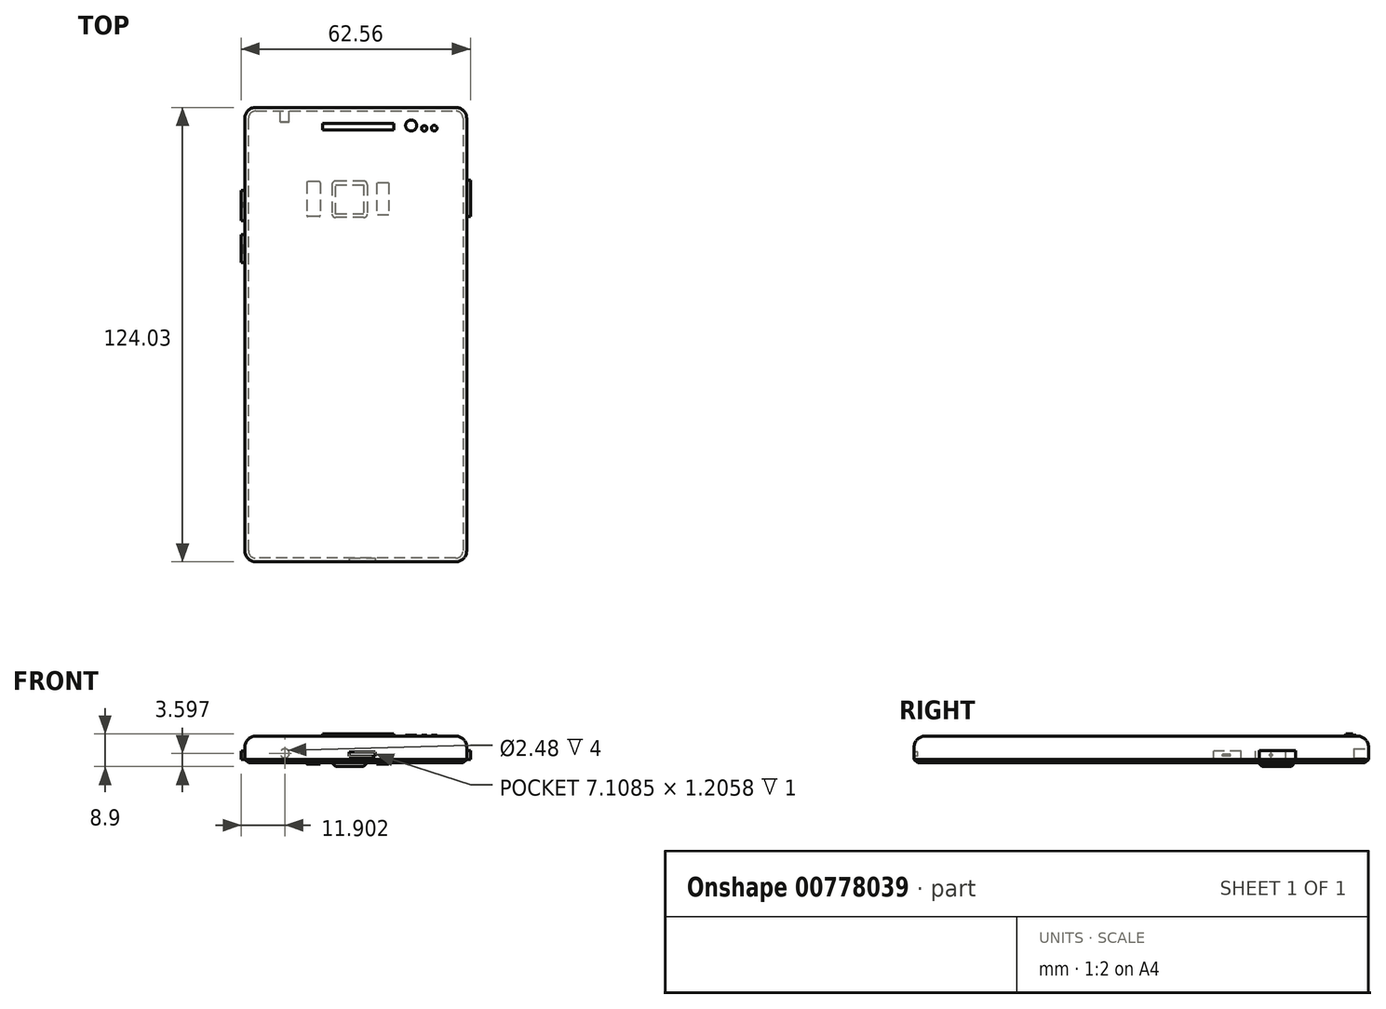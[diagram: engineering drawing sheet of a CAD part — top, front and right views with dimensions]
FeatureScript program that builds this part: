
annotation { "Feature Type Name" : "Feature", "Feature Type Description" : "" }
export const myFeature = defineFeature(function(context is Context, id is Id, definition is map)
    precondition{}
    {
        {
            var Q0;
            Q0=qCreatedBy(makeId("Top.planeOp"),FACE);
            var sketch = newSketch(context, id + "F0", { "sketchPlane" : qUnion([Q0])});
            skLineSegment(sketch, "E0.bottom", {"start": v(-27.17, 60.84) * mm, "end": v(33.39, 60.84) * mm});
            skLineSegment(sketch, "E0.top", {"start": v(-27.17, -63.19) * mm, "end": v(33.39, -63.19) * mm});
            skLineSegment(sketch, "E0.left", {"start": v(-27.17, 60.84) * mm, "end": v(-27.17, -63.19) * mm});
            skLineSegment(sketch, "E0.right", {"start": v(33.39, 60.84) * mm, "end": v(33.39, -63.19) * mm});
            skSolve(sketch);
        }
        {
            var Q0;
            Q0 = qSketchRegion(id + "F0", true);
            extrude(context, id + "F1", {"entities" : qUnion([Q0]), "depth" : 7.3 * mm, "offsetDistance" : 25 * mm});
        }
        {
            var Q0;
            Q0=makeQuery(id+"F1.opExtrude","CAP_EDGE",EDGE,{"disambiguationData":[OSD([sQuery(id+"F0.wireOp",EDGE,"E0.left")])],"isStart":false});
            var Q1;
            Q1=makeQuery(id+"F1.opExtrude","CAP_EDGE",EDGE,{"disambiguationData":[OSD([sQuery(id+"F0.wireOp",EDGE,"E0.right")])],"isStart":false});
            fillet(context, id + "F2", {"entities" : qUnion([Q0, Q1]), "radius" : 3 * mm, "tangentPropagation" : true, "allowEdgeOverflow" : false});
        }
        {
            var Q0;
            Q0=makeQuery(id+"F1.opExtrude","CAP_EDGE",EDGE,{"disambiguationData":[OSD([sQuery(id+"F0.wireOp",EDGE,"E0.bottom")])],"isStart":false});
            fillet(context, id + "F3", {"entities" : qUnion([Q0]), "radius" : 3 * mm, "tangentPropagation" : true, "allowEdgeOverflow" : false});
        }
        {
            var Q0;
            Q0=makeQuery(id+"F1.opExtrude","CAP_EDGE",EDGE,{"disambiguationData":[OSD([sQuery(id+"F0.wireOp",EDGE,"E0.top")])],"isStart":false});
            fillet(context, id + "F4", {"entities" : qUnion([Q0]), "radius" : 3 * mm, "tangentPropagation" : true, "allowEdgeOverflow" : false});
        }
        {
            var Q0;
            Q0=makeQuery(id+"F1.opExtrude","CAP_FACE",FACE,{"disambiguationData":[OSD([sQuery(id+"F0.wireOp",EDGE,"E0.bottom"),sQuery(id+"F0.wireOp",EDGE,"E0.top"),sQuery(id+"F0.wireOp",EDGE,"E0.left"),sQuery(id+"F0.wireOp",EDGE,"E0.right")])],"isStart":false});
            var sketch = newSketch(context, id + "F5", { "sketchPlane" : qUnion([Q0])});
            skLineSegment(sketch, "E1.bottom", {"start": v(-24.17, 57.84) * mm, "end": v(30.39, 57.84) * mm});
            skLineSegment(sketch, "E1.top", {"start": v(-24.17, 53.8) * mm, "end": v(30.39, 53.8) * mm});
            skLineSegment(sketch, "E1.left", {"start": v(-24.17, 57.84) * mm, "end": v(-24.17, 53.8) * mm});
            skLineSegment(sketch, "E1.right", {"start": v(30.39, 57.84) * mm, "end": v(30.39, 53.8) * mm});
            skSolve(sketch);
        }
        {
            var Q0;
            Q0=makeQuery(id+"F5.imprint","IMPRINT",FACE,{"disambiguationData":[TD([[makeQuery(id+"F5.imprint","IMPRINT",EDGE,{"derivedFrom":sQuery(id+"F5.wireOp",EDGE,"E1.bottom")}),1.0]])]});
            var sketch = newSketch(context, id + "F6", { "sketchPlane" : qUnion([Q0])});
            skLineSegment(sketch, "E2.bottom", {"start": v(-5.95, 56.51) * mm, "end": v(13.55, 56.51) * mm});
            skLineSegment(sketch, "E2.top", {"start": v(-5.95, 54.7) * mm, "end": v(13.55, 54.7) * mm});
            skLineSegment(sketch, "E2.left", {"start": v(-5.95, 56.51) * mm, "end": v(-5.95, 54.7) * mm});
            skLineSegment(sketch, "E2.right", {"start": v(13.55, 56.51) * mm, "end": v(13.55, 54.7) * mm});
            skSolve(sketch);
        }
        {
            var Q0;
            Q0=makeQuery(id+"F6.imprint","IMPRINT",FACE,{"disambiguationData":[TD([[makeQuery(id+"F6.imprint","IMPRINT",EDGE,{"derivedFrom":sQuery(id+"F6.wireOp",EDGE,"E2.bottom")}),-1.0]])]});
            extrude(context, id + "F7", {"entities" : qUnion([Q0]), "operationType" : NewBodyOperationType.ADD, "depth" : 0.3 * mm, "offsetDistance" : 25 * mm});
        }
        {
            var Q0;
            Q0=makeQuery(id+"F5.imprint","IMPRINT",FACE,{"disambiguationData":[TD([[makeQuery(id+"F5.imprint","IMPRINT",EDGE,{"derivedFrom":sQuery(id+"F5.wireOp",EDGE,"E1.bottom")}),1.0]])]});
            var sketch = newSketch(context, id + "F8", { "sketchPlane" : qUnion([Q0])});
            skCircle(sketch, "E3", {"center": v(18.23, 55.9) * mm, "radius": 1.51 * mm});
            skCircle(sketch, "E4", {"center": v(21.8, 55.1) * mm, "radius": 0.75 * mm});
            skCircle(sketch, "E5", {"center": v(24.52, 55.17) * mm, "radius": 0.77 * mm});
            skSolve(sketch);
        }
        {
            var Q0;
            Q0=makeQuery(id+"F8.imprint","IMPRINT",FACE,{"disambiguationData":[TD([[makeQuery(id+"F8.imprint","IMPRINT",EDGE,{"derivedFrom":sQuery(id+"F8.wireOp",EDGE,"E3")}),1.0]])]});
            var Q1;
            Q1=makeQuery(id+"F8.imprint","IMPRINT",FACE,{"disambiguationData":[TD([[makeQuery(id+"F8.imprint","IMPRINT",EDGE,{"derivedFrom":sQuery(id+"F8.wireOp",EDGE,"E4")}),1.0]])]});
            var Q2;
            Q2=makeQuery(id+"F8.imprint","IMPRINT",FACE,{"disambiguationData":[TD([[makeQuery(id+"F8.imprint","IMPRINT",EDGE,{"derivedFrom":sQuery(id+"F8.wireOp",EDGE,"E5")}),1.0]])]});
            var Q3;
            Q3=makeQuery(id+"F7.opExtrude","CAP_FACE",FACE,{"disambiguationData":[OSD([sQuery(id+"F6.wireOp",EDGE,"E2.bottom"),sQuery(id+"F6.wireOp",EDGE,"E2.top"),sQuery(id+"F6.wireOp",EDGE,"E2.left"),sQuery(id+"F6.wireOp",EDGE,"E2.right")])],"isStart":false});
            extrude(context, id + "F9", {"entities" : qUnion([Q0, Q1, Q2, Q3]), "operationType" : NewBodyOperationType.ADD, "depth" : 0.3 * mm, "offsetDistance" : 25 * mm});
        }
        {
            var Q0;
            Q0=makeQuery(id+"F1.opExtrude","CAP_EDGE",EDGE,{"disambiguationData":[OSD([sQuery(id+"F0.wireOp",EDGE,"E0.right")])],"isStart":true});
            var Q1;
            Q1=makeQuery(id+"F1.opExtrude","CAP_EDGE",EDGE,{"disambiguationData":[OSD([sQuery(id+"F0.wireOp",EDGE,"E0.bottom")])],"isStart":true});
            var Q2;
            Q2=makeQuery(id+"F1.opExtrude","CAP_EDGE",EDGE,{"disambiguationData":[OSD([sQuery(id+"F0.wireOp",EDGE,"E0.left")])],"isStart":true});
            var Q3;
            Q3=makeQuery(id+"F1.opExtrude","CAP_FACE",FACE,{"disambiguationData":[OSD([sQuery(id+"F0.wireOp",EDGE,"E0.bottom"),sQuery(id+"F0.wireOp",EDGE,"E0.top"),sQuery(id+"F0.wireOp",EDGE,"E0.left"),sQuery(id+"F0.wireOp",EDGE,"E0.right")])],"isStart":true});
            chamfer(context, id + "F10", {"entities" : qUnion([Q0, Q1, Q2, Q3]), "width" : 1 * mm, "tangentPropagation" : true});
        }
        {
            var Q0;
            Q0=makeQuery(id+"F1.opExtrude","CAP_FACE",FACE,{"disambiguationData":[OSD([sQuery(id+"F0.wireOp",EDGE,"E0.bottom"),sQuery(id+"F0.wireOp",EDGE,"E0.top"),sQuery(id+"F0.wireOp",EDGE,"E0.left"),sQuery(id+"F0.wireOp",EDGE,"E0.right")])],"isStart":true});
            var sketch = newSketch(context, id + "F11", { "sketchPlane" : qUnion([Q0])});
            skLineSegment(sketch, "E6.bottom", {"start": v(6.26, -40.74) * mm, "end": v(-3.36, -40.74) * mm});
            skLineSegment(sketch, "E6.top", {"start": v(6.26, -30.76) * mm, "end": v(-3.36, -30.76) * mm});
            skLineSegment(sketch, "E6.left", {"start": v(6.26, -40.74) * mm, "end": v(6.26, -30.76) * mm});
            skLineSegment(sketch, "E6.right", {"start": v(-3.36, -40.74) * mm, "end": v(-3.36, -30.76) * mm});
            skSolve(sketch);
        }
        {
            var Q0;
            Q0 = qSketchRegion(id + "F11", true);
            extrude(context, id + "F12", {"entities" : qUnion([Q0]), "operationType" : NewBodyOperationType.ADD, "depth" : 1 * mm, "offsetDistance" : 25 * mm});
        }
        {
            var Q0;
            Q0=makeQuery(id+"F12.opExtrude","SWEPT_EDGE",EDGE,{"disambiguationData":[OSD([sQuery(id+"F11.wireOp",EDGE,"E6.bottom"),sQuery(id+"F11.wireOp",EDGE,"E6.right")])]});
            var Q1;
            Q1=makeQuery(id+"F12.opExtrude","SWEPT_EDGE",EDGE,{"disambiguationData":[OSD([sQuery(id+"F11.wireOp",EDGE,"E6.top"),sQuery(id+"F11.wireOp",EDGE,"E6.right")])]});
            var Q2;
            Q2=makeQuery(id+"F12.opExtrude","SWEPT_EDGE",EDGE,{"disambiguationData":[OSD([sQuery(id+"F11.wireOp",EDGE,"E6.top"),sQuery(id+"F11.wireOp",EDGE,"E6.left")])]});
            var Q3;
            Q3=makeQuery(id+"F12.opExtrude","SWEPT_EDGE",EDGE,{"disambiguationData":[OSD([sQuery(id+"F11.wireOp",EDGE,"E6.bottom"),sQuery(id+"F11.wireOp",EDGE,"E6.left")])]});
            fillet(context, id + "F13", {"entities" : qUnion([Q0, Q1, Q2, Q3]), "radius" : 1 * mm, "tangentPropagation" : true, "allowEdgeOverflow" : false});
        }
        {
            var Q0;
            Q0=makeQuery(id+"F12.opExtrude","CAP_EDGE",EDGE,{"disambiguationData":[OSD([sQuery(id+"F11.wireOp",EDGE,"E6.left")])],"isStart":false});
            chamfer(context, id + "F14", {"entities" : qUnion([Q0]), "width" : 1 * mm, "tangentPropagation" : true});
        }
        {
            var Q0;
            Q0=makeQuery(id+"F1.opExtrude","CAP_FACE",FACE,{"disambiguationData":[OSD([sQuery(id+"F0.wireOp",EDGE,"E0.bottom"),sQuery(id+"F0.wireOp",EDGE,"E0.top"),sQuery(id+"F0.wireOp",EDGE,"E0.left"),sQuery(id+"F0.wireOp",EDGE,"E0.right")])],"isStart":true});
            var sketch = newSketch(context, id + "F15", { "sketchPlane" : qUnion([Q0])});
            skLineSegment(sketch, "E7.bottom", {"start": v(12.1, -40.16) * mm, "end": v(8.74, -40.16) * mm});
            skLineSegment(sketch, "E7.top", {"start": v(12.1, -31.46) * mm, "end": v(8.74, -31.46) * mm});
            skLineSegment(sketch, "E7.left", {"start": v(12.1, -40.16) * mm, "end": v(12.1, -31.46) * mm});
            skLineSegment(sketch, "E7.right", {"start": v(8.74, -40.16) * mm, "end": v(8.74, -31.46) * mm});
            skSolve(sketch);
        }
        {
            var Q0;
            Q0=makeQuery(id+"F15.imprint","IMPRINT",FACE,{"disambiguationData":[TD([[makeQuery(id+"F15.imprint","IMPRINT",EDGE,{"derivedFrom":sQuery(id+"F15.wireOp",EDGE,"E7.bottom")}),-1.0]])]});
            extrude(context, id + "F16", {"entities" : qUnion([Q0]), "operationType" : NewBodyOperationType.ADD, "depth" : 0.3 * mm, "offsetDistance" : 25 * mm});
        }
        {
            var Q0;
            Q0=makeQuery(id+"F1.opExtrude","CAP_FACE",FACE,{"disambiguationData":[OSD([sQuery(id+"F0.wireOp",EDGE,"E0.bottom"),sQuery(id+"F0.wireOp",EDGE,"E0.top"),sQuery(id+"F0.wireOp",EDGE,"E0.left"),sQuery(id+"F0.wireOp",EDGE,"E0.right")])],"isStart":true});
            var sketch = newSketch(context, id + "F17", { "sketchPlane" : qUnion([Q0])});
            skLineSegment(sketch, "E8.bottom", {"start": v(-6.52, -40.53) * mm, "end": v(-10.26, -40.53) * mm});
            skLineSegment(sketch, "E8.top", {"start": v(-6.52, -31.1) * mm, "end": v(-10.26, -31.1) * mm});
            skLineSegment(sketch, "E8.left", {"start": v(-6.52, -40.53) * mm, "end": v(-6.52, -31.1) * mm});
            skLineSegment(sketch, "E8.right", {"start": v(-10.26, -40.53) * mm, "end": v(-10.26, -31.1) * mm});
            skSolve(sketch);
        }
        {
            var Q0;
            Q0=makeQuery(id+"F17.imprint","IMPRINT",FACE,{"disambiguationData":[TD([[makeQuery(id+"F17.imprint","IMPRINT",EDGE,{"derivedFrom":sQuery(id+"F17.wireOp",EDGE,"E8.bottom")}),-1.0]])]});
            extrude(context, id + "F18", {"entities" : qUnion([Q0]), "operationType" : NewBodyOperationType.ADD, "depth" : 0.3 * mm, "offsetDistance" : 25 * mm});
        }
        {
            var Q0;
            Q0=makeQuery(id+"F18.opExtrude","SWEPT_EDGE",EDGE,{"disambiguationData":[OSD([sQuery(id+"F17.wireOp",EDGE,"E8.bottom"),sQuery(id+"F17.wireOp",EDGE,"E8.right")])]});
            var Q1;
            Q1=makeQuery(id+"F18.opExtrude","SWEPT_EDGE",EDGE,{"disambiguationData":[OSD([sQuery(id+"F17.wireOp",EDGE,"E8.top"),sQuery(id+"F17.wireOp",EDGE,"E8.right")])]});
            var Q2;
            Q2=makeQuery(id+"F18.opExtrude","SWEPT_EDGE",EDGE,{"disambiguationData":[OSD([sQuery(id+"F17.wireOp",EDGE,"E8.top"),sQuery(id+"F17.wireOp",EDGE,"E8.left")])]});
            var Q3;
            Q3=makeQuery(id+"F18.opExtrude","SWEPT_EDGE",EDGE,{"disambiguationData":[OSD([sQuery(id+"F17.wireOp",EDGE,"E8.bottom"),sQuery(id+"F17.wireOp",EDGE,"E8.left")])]});
            fillet(context, id + "F19", {"entities" : qUnion([Q0, Q1, Q2, Q3]), "radius" : 0.3 * mm, "tangentPropagation" : true, "allowEdgeOverflow" : false});
        }
        {
            var Q0;
            Q0=makeQuery(id+"F1.opExtrude","SWEPT_FACE",FACE,{"disambiguationData":[OSD([sQuery(id+"F0.wireOp",EDGE,"E0.right")])]});
            var sketch = newSketch(context, id + "F20", { "sketchPlane" : qUnion([Q0])});
            skLineSegment(sketch, "E9.bottom", {"start": v(31.06, 1) * mm, "end": v(40.96, 1) * mm});
            skLineSegment(sketch, "E9.top", {"start": v(31.06, 3.39) * mm, "end": v(40.96, 3.39) * mm});
            skLineSegment(sketch, "E9.left", {"start": v(31.06, 1) * mm, "end": v(31.06, 3.39) * mm});
            skLineSegment(sketch, "E9.right", {"start": v(40.96, 1) * mm, "end": v(40.96, 3.39) * mm});
            skSolve(sketch);
        }
        {
            var Q0;
            Q0 = qSketchRegion(id + "F20", true);
            extrude(context, id + "F21", {"entities" : qUnion([Q0]), "operationType" : NewBodyOperationType.ADD, "depth" : 1 * mm, "offsetDistance" : 25 * mm});
        }
        {
            var Q0;
            Q0=makeQuery(id+"F1.opExtrude","SWEPT_FACE",FACE,{"disambiguationData":[OSD([sQuery(id+"F0.wireOp",EDGE,"E0.left")])]});
            var sketch = newSketch(context, id + "F22", { "sketchPlane" : qUnion([Q0])});
            skLineSegment(sketch, "E10.bottom", {"start": v(-38.2, 1) * mm, "end": v(-29.94, 1) * mm});
            skLineSegment(sketch, "E10.top", {"start": v(-38.2, 3.3) * mm, "end": v(-29.94, 3.3) * mm});
            skLineSegment(sketch, "E10.left", {"start": v(-38.2, 1) * mm, "end": v(-38.2, 3.3) * mm});
            skLineSegment(sketch, "E10.right", {"start": v(-29.94, 1) * mm, "end": v(-29.94, 3.3) * mm});
            skLineSegment(sketch, "E11.bottom", {"start": v(-26.06, 1) * mm, "end": v(-18.51, 1) * mm});
            skLineSegment(sketch, "E11.top", {"start": v(-26.06, 3.3) * mm, "end": v(-18.51, 3.3) * mm});
            skLineSegment(sketch, "E11.left", {"start": v(-26.06, 1) * mm, "end": v(-26.06, 3.3) * mm});
            skLineSegment(sketch, "E11.right", {"start": v(-18.51, 1) * mm, "end": v(-18.51, 3.3) * mm});
            skSolve(sketch);
        }
        {
            var Q0;
            Q0 = qSketchRegion(id + "F22", true);
            extrude(context, id + "F23", {"entities" : qUnion([Q0]), "operationType" : NewBodyOperationType.ADD, "depth" : 1 * mm, "offsetDistance" : 25 * mm});
        }
        {
            var Q0;
            Q0=makeQuery(id+"F23.opExtrude","CAP_FACE",FACE,{"disambiguationData":[OSD([sQuery(id+"F22.wireOp",EDGE,"E10.bottom"),sQuery(id+"F22.wireOp",EDGE,"E10.top"),sQuery(id+"F22.wireOp",EDGE,"E10.left"),sQuery(id+"F22.wireOp",EDGE,"E10.right")])],"isStart":false});
            var sketch = newSketch(context, id + "F24", { "sketchPlane" : qUnion([Q0])});
            skText(sketch, "E12", { "text": "+", "fontName": "OpenSans-Regular.ttf"});
            const initialGuessF24  = {"E12": [-0.03485, 0.00133, 1, 0, 0.00167]};
            skSetInitialGuess(sketch, initialGuessF24);
            skSolve(sketch);
        }
        {
            var Q0;
            Q0 = qSketchRegion(id + "F24", true);
            extrude(context, id + "F25", {"entities" : qUnion([Q0]), "operationType" : NewBodyOperationType.REMOVE, "oppositeDirection" : true, "depth" : 0.5 * mm, "offsetDistance" : 25 * mm});
        }
        {
            var Q0;
            Q0=makeQuery(id+"F23.opExtrude","CAP_FACE",FACE,{"disambiguationData":[OSD([sQuery(id+"F22.wireOp",EDGE,"E11.bottom"),sQuery(id+"F22.wireOp",EDGE,"E11.top"),sQuery(id+"F22.wireOp",EDGE,"E11.left"),sQuery(id+"F22.wireOp",EDGE,"E11.right")])],"isStart":false});
            var sketch = newSketch(context, id + "F26", { "sketchPlane" : qUnion([Q0])});
            skLineSegment(sketch, "E13.bottom", {"start": v(-23.2, 1.83) * mm, "end": v(-21, 1.83) * mm});
            skLineSegment(sketch, "E13.top", {"start": v(-23.2, 2.37) * mm, "end": v(-21, 2.37) * mm});
            skLineSegment(sketch, "E13.left", {"start": v(-23.2, 1.83) * mm, "end": v(-23.2, 2.37) * mm});
            skLineSegment(sketch, "E13.right", {"start": v(-21, 1.83) * mm, "end": v(-21, 2.37) * mm});
            skSolve(sketch);
        }
        {
            var Q0;
            Q0 = qSketchRegion(id + "F26", true);
            extrude(context, id + "F27", {"entities" : qUnion([Q0]), "operationType" : NewBodyOperationType.REMOVE, "oppositeDirection" : true, "depth" : 0.5 * mm, "offsetDistance" : 25 * mm});
        }
        {
            var Q0;
            Q0=makeQuery(id+"F1.opExtrude","SWEPT_FACE",FACE,{"disambiguationData":[OSD([sQuery(id+"F0.wireOp",EDGE,"E0.top")])]});
            var sketch = newSketch(context, id + "F28", { "sketchPlane" : qUnion([Q0])});
            skLineSegment(sketch, "E14.bottom", {"start": v(1.36, 1.82) * mm, "end": v(8.47, 1.82) * mm});
            skLineSegment(sketch, "E14.top", {"start": v(1.36, 3.03) * mm, "end": v(8.47, 3.03) * mm});
            skLineSegment(sketch, "E14.left", {"start": v(1.36, 1.82) * mm, "end": v(1.36, 3.03) * mm});
            skLineSegment(sketch, "E14.right", {"start": v(8.47, 1.82) * mm, "end": v(8.47, 3.03) * mm});
            skSolve(sketch);
        }
        {
            var Q0;
            Q0 = qSketchRegion(id + "F28", true);
            extrude(context, id + "F29", {"entities" : qUnion([Q0]), "operationType" : NewBodyOperationType.REMOVE, "oppositeDirection" : true, "depth" : 1 * mm, "offsetDistance" : 25 * mm});
        }
        {
            var Q0;
            Q0=makeQuery(id+"F1.opExtrude","SWEPT_FACE",FACE,{"disambiguationData":[OSD([sQuery(id+"F0.wireOp",EDGE,"E0.bottom")])]});
            var sketch = newSketch(context, id + "F30", { "sketchPlane" : qUnion([Q0])});
            skCircle(sketch, "E15", {"center": v(16.27, 2.6) * mm, "radius": 1.24 * mm});
            skSolve(sketch);
        }
        {
            var Q0;
            Q0 = qSketchRegion(id + "F30", true);
            extrude(context, id + "F31", {"entities" : qUnion([Q0]), "operationType" : NewBodyOperationType.REMOVE, "oppositeDirection" : true, "depth" : 4 * mm, "offsetDistance" : 25 * mm});
        }
    });
